# Revit family: Table-Teknion-Zones_ZNTWB-R2015
name_source: partatom
category: Furniture
revit_build: Autodesk Revit Architecture 2015 (Build: 20140322_1515(x64)
units: mm (PartAtom-declared; Revit-internal decimal feet)

## types (3) — shared parameters
Assembly Code = E2020200
Depth = 48"
Height = 25"
Leg Depth = 37 3/32"
Leg Width = 37 3/32"
Manufacturer = Teknion
Manufacturer Fax = 416.661.4586
Part Number = ZNTWB
Power Pill Two Power Two USB Modules = No
Product Documentation Link = http://www.teknion.com
Product Line = Zones
Product Page URL = http://www.teknion.com
Series = Zones
Sustainability Data = http://www.teknion.com
URL = http://www.teknion.com
Warranty = http://www.teknion.com
Width = 48"

## per-type parameters (varying)
| type | Apparent Load | Connector Description | Description | Model | Voltage | With Center Light | With Power Pill |
| Table 48", with Center Light | 21 VA | Power Connector | Square Dialogue Workshop Table, 48"d, with Center Light Cut-Out | ZNTWB48L | 120 V | Yes | No |
| Table 48'' | 0 VA | Without Power Connector | Square Dialogue Workshop Table, 48"d, without Cut-Out | ZNTWB48N | 0 V | No | No |
| Table 48", with Power Pill | 0 VA | Power Connector | Square Dialogue Workshop Table, 48"d, With Center Pill Cut-Out | ZNTWB48P | 120 V | No | Yes |

## geometry (parser evidence)
native form markers: Blend x328, Sweep x17
no freeform markers — native parametric forms only
